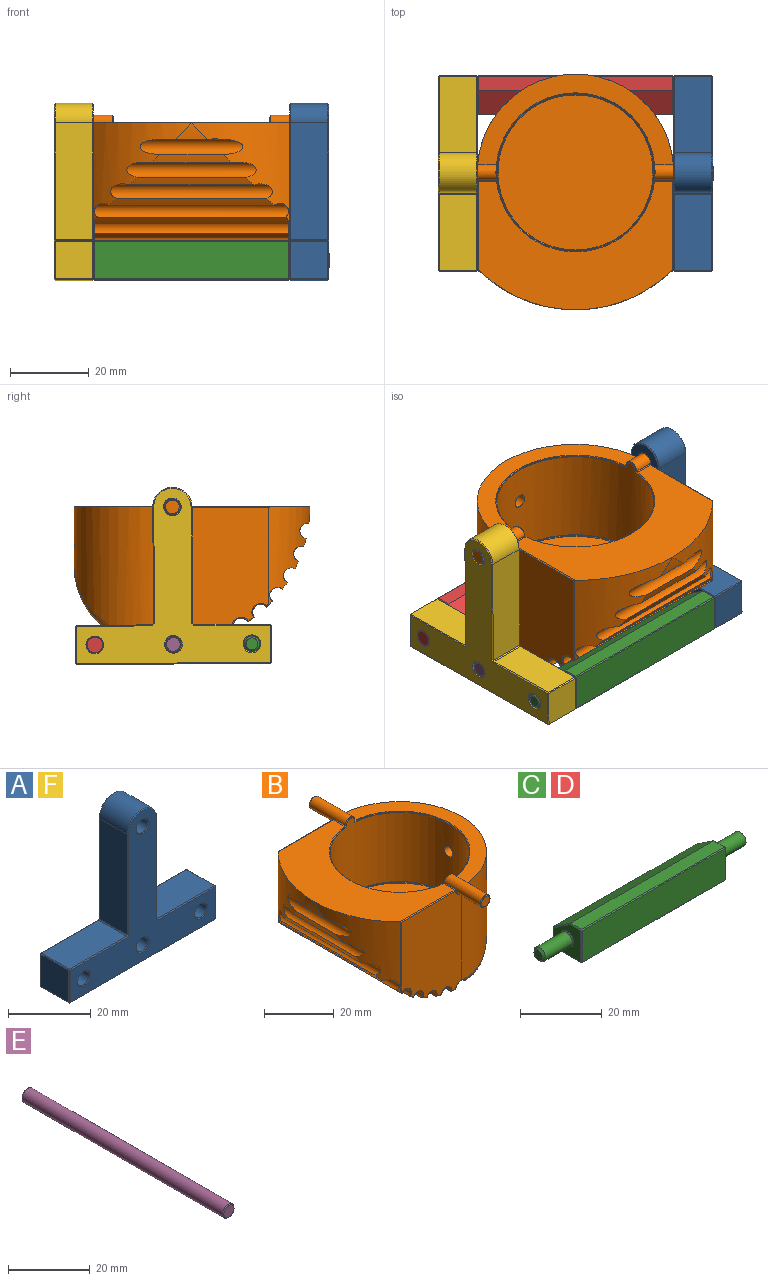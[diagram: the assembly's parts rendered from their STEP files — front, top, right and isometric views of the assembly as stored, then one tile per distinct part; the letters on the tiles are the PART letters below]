
ASSEMBLY  parts=6 mates=6
PART A: 56 faces, bbox 50x10x45 mm
  f0: plane 49.5x44.5mm, normal (0,-1,0), area 729.7mm2, adj f14,f17,f18,f21,f22,f27,f31,f32
  f1: plane 49.5x44.5mm, normal (0,1,0), area 729.7mm2, adj f16,f19,f20,f24,f25,f30,f34,f35
  f2: plane 29.75x9.5mm, normal (1,0,0), area 282.6mm2, adj f3,f14,f15,f16
  f3: cylinder r=5mm len=10mm, axis (0,1,0), area 149.2mm2, adj f2,f4,f17,f20
  f4: plane 29.75x9.5mm, normal (-1,0,0), area 282.6mm2, adj f3,f21,f25,f26
  f5: plane 19.5x9.5mm, normal (0,0,1), area 185.2mm2, adj f26,f31,f35,f36
  f6: plane 9.5x9.5mm, normal (-1,0,0), area 90.3mm2, adj f36,f41,f44,f47
  f7: plane 49.5x9.5mm, normal (0,0,-1), area 470.2mm2, adj f33,f42,f43,f47
  f8: plane 9.5x9.5mm, normal (1,0,0), area 90.3mm2, adj f23,f32,f33,f34
  f9: cylinder r=2mm len=9.5mm, axis (0,1,0), area 119.4mm2, adj f48,f52
  f10: cylinder r=2mm len=9.5mm, axis (0,1,0), area 119.4mm2, adj f49,f53
  f11: cylinder r=2mm len=9.5mm, axis (0,1,0), area 119.4mm2, adj f50,f54
  f12: plane 19.5x9.5mm, normal (0,0,1), area 185.2mm2, adj f15,f22,f23,f24
  f13: cylinder r=2mm len=9.5mm, axis (0,1,0), area 119.4mm2, adj f51,f55
  f14: plane 29.75x0.25mm, normal (0.71,-0.71,0), area 10.5mm2, adj f0,f2,f17,f18
  f15: plane 9.5x0.25mm, normal (0.71,0,0.71), area 3.4mm2, adj f2,f12,f18,f19
  f16: plane 29.75x0.25mm, normal (0.71,0.71,0), area 10.5mm2, adj f1,f2,f19,f20
  f17: cone r=4.75mm half-angle=45deg, axis (0,1,0), area 5.4mm2, adj f0,f3,f14,f21
  f18: plane 0.5x0.5mm, normal (0.58,-0.58,0.58), area 0.2mm2, adj f0,f14,f15,f22
  f19: plane 0.5x0.5mm, normal (0.58,0.58,0.58), area 0.2mm2, adj f1,f15,f16,f24
  f20: cone r=5mm half-angle=45deg, axis (0,-1,0), area 5.4mm2, adj f1,f3,f16,f25
  f21: plane 29.75x0.25mm, normal (-0.71,-0.71,0), area 10.5mm2, adj f0,f4,f17,f27
  f22: plane 19.5x0.25mm, normal (0,-0.71,0.71), area 6.9mm2, adj f0,f12,f18,f28
  f23: plane 9.5x0.25mm, normal (0.71,0,0.71), area 3.4mm2, adj f8,f12,f28,f29
  f24: plane 19.5x0.25mm, normal (0,0.71,0.71), area 6.9mm2, adj f1,f12,f19,f29
  f25: plane 29.75x0.25mm, normal (-0.71,0.71,0), area 10.5mm2, adj f1,f4,f20,f30
  f26: plane 9.5x0.25mm, normal (-0.71,0,0.71), area 3.4mm2, adj f4,f5,f27,f30
  f27: plane 0.5x0.5mm, normal (-0.58,-0.58,0.58), area 0.2mm2, adj f0,f21,f26,f31
  f28: plane 0.25x0.25mm, normal (0.58,-0.58,0.58), area 0.1mm2, adj f22,f23,f32
  f29: plane 0.25x0.25mm, normal (0.58,0.58,0.58), area 0.1mm2, adj f23,f24,f34
  f30: plane 0.5x0.5mm, normal (-0.58,0.58,0.58), area 0.2mm2, adj f1,f25,f26,f35
  f31: plane 19.5x0.25mm, normal (0,-0.71,0.71), area 6.9mm2, adj f0,f5,f27,f37
  f32: plane 9.5x0.25mm, normal (0.71,-0.71,0), area 3.4mm2, adj f0,f8,f28,f38
  f33: plane 9.5x0.25mm, normal (0.71,0,-0.71), area 3.4mm2, adj f7,f8,f38,f39
  f34: plane 9.5x0.25mm, normal (0.71,0.71,0), area 3.4mm2, adj f1,f8,f29,f39
  f35: plane 19.5x0.25mm, normal (0,0.71,0.71), area 6.9mm2, adj f1,f5,f30,f40
  f36: plane 9.5x0.25mm, normal (-0.71,0,0.71), area 3.4mm2, adj f5,f6,f37,f40
  f37: plane 0.25x0.25mm, normal (-0.58,-0.58,0.58), area 0.1mm2, adj f31,f36,f41
  f38: plane 0.25x0.25mm, normal (0.58,-0.58,-0.58), area 0.1mm2, adj f32,f33,f42
  f39: plane 0.25x0.25mm, normal (0.58,0.58,-0.58), area 0.1mm2, adj f33,f34,f43
  f40: plane 0.25x0.25mm, normal (-0.58,0.58,0.58), area 0.1mm2, adj f35,f36,f44
  f41: plane 9.5x0.25mm, normal (-0.71,-0.71,0), area 3.4mm2, adj f0,f6,f37,f45
  f42: plane 49.5x0.25mm, normal (0,-0.71,-0.71), area 17.5mm2, adj f0,f7,f38,f45
  f43: plane 49.5x0.25mm, normal (0,0.71,-0.71), area 17.5mm2, adj f1,f7,f39,f46
  f44: plane 9.5x0.25mm, normal (-0.71,0.71,0), area 3.4mm2, adj f1,f6,f40,f46
  f45: plane 0.25x0.25mm, normal (-0.58,-0.58,-0.58), area 0.1mm2, adj f41,f42,f47
  f46: plane 0.25x0.25mm, normal (-0.58,0.58,-0.58), area 0.1mm2, adj f43,f44,f47
  f47: plane 9.5x0.25mm, normal (-0.71,0,-0.71), area 3.4mm2, adj f6,f7,f45,f46
  f48: cone r=2mm half-angle=45deg, axis (0,1,0), area 4.7mm2, adj f1,f9
  f49: cone r=2.25mm half-angle=45deg, axis (0,1,0), area 4.7mm2, adj f1,f10
  f50: cone r=2.25mm half-angle=45deg, axis (0,1,0), area 4.7mm2, adj f1,f11
  f51: cone r=2.25mm half-angle=45deg, axis (0,1,0), area 4.7mm2, adj f1,f13
  f52: cone r=2.25mm half-angle=45deg, axis (0,-1,0), area 4.7mm2, adj f0,f9
  f53: cone r=2mm half-angle=45deg, axis (0,-1,0), area 4.7mm2, adj f0,f10
  f54: cone r=2mm half-angle=45deg, axis (0,-1,0), area 4.7mm2, adj f0,f11
  f55: cone r=2mm half-angle=45deg, axis (0,-1,0), area 4.7mm2, adj f0,f13
PART B: 89 faces, bbox 60x70x37.2 mm
  f0: cylinder r=25mm len=50mm, axis (0,0,1), area 2123.7mm2, adj f12,f16,f17,f45,f61,f62,f78,f79
  f1: cylinder r=20mm len=40mm, axis (0,0,1), area 3054.9mm2, adj f2,f30,f31,f32,f33,f34,f88
  f2: cylinder r=20mm len=0.7mm, axis (0,0,1), area 0mm2, adj f1,f32
  f3: cylinder r=35mm len=8.2mm, axis (0,1,0), area 16.8mm2, adj f20,f21,f44
  f4: cylinder r=35mm len=20.15mm, axis (0,1,0), area 38.2mm2, adj f20,f21,f43,f44
  f5: cylinder r=35mm len=31.48mm, axis (0,1,0), area 62.3mm2, adj f20,f21,f42,f43
  f6: cylinder r=35mm len=41.86mm, axis (0,1,0), area 84.6mm2, adj f20,f21,f41,f42
  f7: cylinder r=35mm len=49.5mm, axis (0,1,0), area 103.6mm2, adj f20,f21,f40,f41,f51,f68
  f8: cylinder r=35mm len=49.5mm, axis (0,1,0), area 104.4mm2, adj f39,f40,f53,f70
  f9: cylinder r=35mm len=49.5mm, axis (0,1,0), area 104.4mm2, adj f38,f39,f55,f72
  f10: cylinder r=35mm len=49.5mm, axis (0,1,0), area 104.4mm2, adj f37,f38,f57,f74
  f11: plane 45.48x1.54mm, normal (0,0,-1), area 69.4mm2, adj f18,f81,f84,f87
  f12: plane 50.31x23.03mm, normal (0,0,1), area 318.6mm2, adj f0,f22,f24,f25,f28,f32,f45,f62
  f13: cone r=20mm half-angle=45deg, axis (0,0,1), area 14.8mm2, adj f14,f25,f30,f32
  f14: plane 49.5x33.03mm, normal (0,0,1), area 910.3mm2, adj f13,f20,f21,f25,f32,f47,f49,f63
  f15: cylinder r=35mm len=49.5mm, axis (0,1,0), area 104.4mm2, adj f36,f37,f59,f76
  f16: plane 34.43x24.39mm, normal (0,1,0), area 731.9mm2, adj f0,f46,f49,f50,f51,f52,f53,f54
  f17: plane 34.43x24.39mm, normal (0,-1,0), area 731.9mm2, adj f0,f64,f66,f67,f68,f69,f70,f71
  f18: cylinder r=20mm len=44.9mm, axis (0,1,0), area 705.3mm2, adj f11,f79,f80
  f19: plane 39.5x39.5mm, normal (0,0,1), area 1225.4mm2, adj f26
  f20: cylinder r=35mm len=24.93mm, axis (0,0,1), area 304.3mm2, adj f3,f4,f5,f6,f7,f14,f41,f42
  f21: cylinder r=35mm len=24.93mm, axis (0,0,1), area 304.2mm2, adj f3,f4,f5,f6,f7,f14,f41,f42
  f22: cylinder r=2mm len=14.58mm, axis (0,1,0), area 150.4mm2, adj f12,f25,f27,f62,f63,f64,f65
  f23: plane 3.5x3.5mm, normal (0,-1,0), area 9.6mm2, adj f27
  f24: cone r=20mm half-angle=45deg, axis (0,0,1), area 14.8mm2, adj f12,f25,f32,f33
  f25: bspline ~4.7x2.91mm, area 1.6mm2, adj f12,f13,f14,f22,f24,f31,f63
  f26: cone r=19.75mm half-angle=45deg, axis (0,0,1), area 31.2mm2, adj f19,f34
  f27: cone r=1.75mm half-angle=45deg, axis (0,1,0), area 4.2mm2, adj f22,f23
  f28: cylinder r=2mm len=14.58mm, axis (0,-1,0), area 150.4mm2, adj f12,f32,f35,f45,f46,f47,f48
  f29: plane 3.5x3.5mm, normal (0,1,0), area 9.6mm2, adj f35
  f30: cone r=20mm half-angle=22.5deg, axis (0,0,1), area 11.4mm2, adj f1,f13,f31,f32
  f31: bspline ~3.61x2.21mm, area 1.1mm2, adj f1,f25,f30,f33
  f32: bspline ~4.71x3.04mm, area 2.2mm2, adj f1,f2,f12,f13,f14,f24,f28,f30
  f33: cone r=20mm half-angle=22.5deg, axis (0,0,1), area 11.4mm2, adj f1,f24,f31,f32
  f34: cone r=20mm half-angle=22.5deg, axis (0,0,1), area 24mm2, adj f1,f26
  f35: cone r=2mm half-angle=45deg, axis (0,-1,0), area 4.2mm2, adj f28,f29
  f36: cylinder r=2mm len=49.5mm, axis (0,-1,0), area 256mm2, adj f15,f60,f61,f77,f78,f82,f83,f87
  f37: cylinder r=2mm len=49.5mm, axis (0,-1,0), area 305.4mm2, adj f10,f15,f58,f75
  f38: cylinder r=2mm len=49.5mm, axis (0,-1,0), area 305.4mm2, adj f9,f10,f56,f73
  f39: cylinder r=2mm len=49.5mm, axis (0,-1,0), area 305.4mm2, adj f8,f9,f54,f71
  f40: cylinder r=2mm len=49.5mm, axis (0,-1,0), area 305.4mm2, adj f7,f8,f52,f69
  f41: cylinder r=2mm len=47.98mm, axis (0,-1,0), area 277.1mm2, adj f6,f7,f20,f21
  f42: cylinder r=2mm len=38.41mm, axis (0,-1,0), area 215.6mm2, adj f5,f6,f20,f21
  f43: cylinder r=2mm len=32.92mm, axis (0,-1,0), area 182.4mm2, adj f4,f5,f20,f21
  f44: cylinder r=2mm len=26.14mm, axis (0,-1,0), area 134.1mm2, adj f3,f4,f20,f21
  f45: bspline ~2.63x2.56mm, area 1.3mm2, adj f0,f12,f28,f46
  f46: torus R=2.25mm, axis (0,-1,0), area 1.2mm2, adj f16,f28,f45,f48
  f47: cylinder r=0.25mm len=4.57mm, axis (0,-1,0), area 1.6mm2, adj f14,f28,f32,f48
  f48: bspline ~0.58x0.54mm, area 0.2mm2, adj f28,f46,f47,f49
  f49: cylinder r=0.25mm len=22.51mm, axis (-1,0,0), area 8.8mm2, adj f14,f16,f21,f48,f50
  f50: cylinder r=0.25mm len=24.75mm, axis (0,0,1), area 4.8mm2, adj f16,f21,f49,f51
  f51: torus R=34.75mm, axis (0,-1,0), area 0.3mm2, adj f7,f16,f21,f50,f52
  f52: torus R=2.25mm, axis (0,-1,0), area 2.4mm2, adj f16,f40,f51,f53
  f53: torus R=34.75mm, axis (0,-1,0), area 0.7mm2, adj f8,f16,f52,f54
  f54: torus R=2.25mm, axis (0,-1,0), area 2.4mm2, adj f16,f39,f53,f55
  f55: torus R=34.75mm, axis (0,-1,0), area 0.7mm2, adj f9,f16,f54,f56
  f56: torus R=2.25mm, axis (0,-1,0), area 2.4mm2, adj f16,f38,f55,f57
  f57: torus R=34.75mm, axis (0,-1,0), area 0.7mm2, adj f10,f16,f56,f58
  f58: torus R=2.25mm, axis (0,-1,0), area 2.4mm2, adj f16,f37,f57,f59
  f59: torus R=34.75mm, axis (0,-1,0), area 0.7mm2, adj f15,f16,f58,f60
  f60: torus R=2.25mm, axis (0,-1,0), area 1.2mm2, adj f16,f36,f59,f61
  f61: bspline ~1.34x0.56mm, area 0.4mm2, adj f0,f36,f60,f82
  f62: bspline ~2.63x2.56mm, area 1.3mm2, adj f0,f12,f22,f64
  f63: cylinder r=0.25mm len=4.57mm, axis (0,1,0), area 1.6mm2, adj f14,f22,f25,f65
  f64: torus R=2.25mm, axis (0,-1,0), area 1.2mm2, adj f17,f22,f62,f65
  f65: bspline ~0.61x0.52mm, area 0.2mm2, adj f22,f63,f64,f66
  f66: cylinder r=0.25mm len=22.51mm, axis (1,0,0), area 8.8mm2, adj f14,f17,f20,f65,f67
  f67: cylinder r=0.25mm len=24.75mm, axis (0,0,1), area 4.8mm2, adj f17,f20,f66,f68
  f68: torus R=34.75mm, axis (0,-1,0), area 0.3mm2, adj f7,f17,f20,f67,f69
  f69: torus R=2.25mm, axis (0,-1,0), area 2.4mm2, adj f17,f40,f68,f70
  f70: torus R=34.75mm, axis (0,-1,0), area 0.7mm2, adj f8,f17,f69,f71
  f71: torus R=2.25mm, axis (0,-1,0), area 2.4mm2, adj f17,f39,f70,f72
  f72: torus R=34.75mm, axis (0,-1,0), area 0.7mm2, adj f9,f17,f71,f73
  f73: torus R=2.25mm, axis (0,-1,0), area 2.4mm2, adj f17,f38,f72,f74
  f74: torus R=34.75mm, axis (0,-1,0), area 0.7mm2, adj f10,f17,f73,f75
  f75: torus R=2.25mm, axis (0,-1,0), area 2.4mm2, adj f17,f37,f74,f76
  f76: torus R=34.75mm, axis (0,-1,0), area 0.7mm2, adj f15,f17,f75,f77
  f77: torus R=2.25mm, axis (0,-1,0), area 1.2mm2, adj f17,f36,f76,f78
  f78: bspline ~1.34x0.56mm, area 0.4mm2, adj f0,f36,f77,f83
  f79: bspline ~24.62x20.91mm, area 46.2mm2, adj f0,f18,f81
  f80: bspline ~24.98x23.64mm, area 46.2mm2, adj f0,f18,f84
  f81: torus R=23mm, axis (0,0,1), area 9.4mm2, adj f0,f11,f79,f82,f85
  f82: bspline ~1.6x1.57mm, area 0.5mm2, adj f36,f61,f81,f85
  f83: bspline ~1.6x1.57mm, area 0.5mm2, adj f36,f78,f84,f86
  f84: torus R=23mm, axis (0,0,1), area 9.4mm2, adj f0,f11,f80,f83,f86
  f85: bspline ~2.06x1.87mm, area 0.3mm2, adj f81,f82,f87
  f86: bspline ~2.06x1.87mm, area 0.3mm2, adj f83,f84,f87
  f87: cylinder r=2mm len=48.88mm, axis (0,-1,0), area 98.8mm2, adj f11,f36,f85,f86
  f88: cylinder r=1.7mm len=5mm, axis (1,0,0), area 53.4mm2, adj f0,f1
PART C: 33 faces, bbox 70x10x10 mm
  f0: plane 49.5x9.5mm, normal (0,0,-1), area 470.2mm2, adj f19,f24,f27,f30
  f1: plane 9.5x9.5mm, normal (1,0,0), area 63mm2, adj f15,f16,f21,f24,f25,f31
  f2: plane 49.5x3.75mm, normal (0,0,1), area 185.6mm2, adj f11,f12,f16,f17
  f3: plane 9.5x9.5mm, normal (-1,0,0), area 63mm2, adj f17,f18,f22,f26,f27,f32
  f4: plane 49.5x9.5mm, normal (0,-1,0), area 470.2mm2, adj f12,f15,f18,f19
  f5: plane 49.5x5.75mm, normal (0,1,0), area 284.6mm2, adj f11,f25,f26,f30
  f6: cylinder r=2mm len=9.25mm, axis (1,0,0), area 116.2mm2, adj f8,f32
  f7: plane 3x3mm, normal (-1,0,0), area 7.1mm2, adj f8
  f8: cone r=1.5mm half-angle=45deg, axis (1,0,0), area 7.8mm2, adj f6,f7
  f9: cylinder r=2mm len=9.75mm, axis (-1,0,0), area 122.5mm2, adj f10,f31
  f10: plane 4x4mm, normal (1,0,0), area 12.6mm2, adj f9
  f11: plane 49.5x6mm, normal (0,0.55,0.83), area 356.9mm2, adj f2,f5,f21,f22
  f12: plane 49.5x0.25mm, normal (0,-0.71,0.71), area 17.5mm2, adj f2,f4,f13,f14
  f13: plane 0.25x0.25mm, normal (0.58,-0.58,0.58), area 0.1mm2, adj f12,f15,f16
  f14: plane 0.25x0.25mm, normal (-0.58,-0.58,0.58), area 0.1mm2, adj f12,f17,f18
  f15: plane 9.5x0.25mm, normal (0.71,-0.71,0), area 3.4mm2, adj f1,f4,f13,f20
  f16: plane 3.75x0.25mm, normal (0.71,0,0.71), area 1.3mm2, adj f1,f2,f13,f21
  f17: plane 3.75x0.25mm, normal (-0.71,0,0.71), area 1.3mm2, adj f2,f3,f14,f22
  f18: plane 9.5x0.25mm, normal (-0.71,-0.71,0), area 3.4mm2, adj f3,f4,f14,f23
  f19: plane 49.5x0.25mm, normal (0,-0.71,-0.71), area 17.5mm2, adj f0,f4,f20,f23
  f20: plane 0.25x0.25mm, normal (0.58,-0.58,-0.58), area 0.1mm2, adj f15,f19,f24
  f21: plane 6.08x4.13mm, normal (0.71,0.39,0.59), area 2.5mm2, adj f1,f11,f16,f25
  f22: plane 6.08x4.13mm, normal (-0.71,0.39,0.59), area 2.5mm2, adj f3,f11,f17,f26
  f23: plane 0.25x0.25mm, normal (-0.58,-0.58,-0.58), area 0.1mm2, adj f18,f19,f27
  f24: plane 9.5x0.25mm, normal (0.71,0,-0.71), area 3.4mm2, adj f0,f1,f20,f28
  f25: plane 5.75x0.25mm, normal (0.71,0.71,0), area 2mm2, adj f1,f5,f21,f28
  f26: plane 5.75x0.25mm, normal (-0.71,0.71,0), area 2mm2, adj f3,f5,f22,f29
  f27: plane 9.5x0.25mm, normal (-0.71,0,-0.71), area 3.4mm2, adj f0,f3,f23,f29
  f28: plane 0.25x0.25mm, normal (0.58,0.58,-0.58), area 0.1mm2, adj f24,f25,f30
  f29: plane 0.25x0.25mm, normal (-0.58,0.58,-0.58), area 0.1mm2, adj f26,f27,f30
  f30: plane 49.5x0.25mm, normal (0,0.71,-0.71), area 17.5mm2, adj f0,f5,f28,f29
  f31: cone r=2.25mm half-angle=45deg, axis (-1,0,0), area 4.7mm2, adj f1,f9
  f32: cone r=2mm half-angle=45deg, axis (1,0,0), area 4.7mm2, adj f3,f6
PART D: same geometry as C
PART E: 5 faces, bbox 4x70x4 mm
  f0: cylinder r=2mm len=69.5mm, axis (0,1,0), area 873.4mm2, adj f3,f4
  f1: plane 3.5x3.5mm, normal (0,-1,0), area 9.6mm2, adj f3
  f2: plane 3.5x3.5mm, normal (0,1,0), area 9.6mm2, adj f4
  f3: cone r=1.75mm half-angle=45deg, axis (0,1,0), area 4.2mm2, adj f0,f1
  f4: cone r=2mm half-angle=45deg, axis (0,-1,0), area 4.2mm2, adj f0,f2
PART F: same geometry as A
PLACE A rot(axis=(0,0,1),90deg) t=(52.06,0,19.85)mm fixed
PLACE B rot(axis=(0,0,1),90deg) t=(22.06,0,19.85)mm
PLACE C rot(axis=(-1,0,0),0.4deg) t=(22.06,-20.25,-15.01)mm
PLACE D rot(axis=(0,0,1),180deg) t=(22.06,19.75,-15.3)mm
PLACE E rot(axis=(0,0,1),90deg) t=(22.31,-0.25,-15.15)mm
PLACE F rot(axis=(0,0,1),90deg) t=(-7.94,0,19.85)mm
MATE fastened D.f6 <-> A.f9  axis (1,0,0) through (47.06,19.75,-15.3)mm
MATE fastened C.f6 <-> A.f10  axis (1,0,0) through (47.06,-20.25,-15.01)mm
MATE revolute F.f13 <-> B.f22  axis (1,0,0) through (-2.94,0,19.85)mm
MATE slider E.f0 <-> A.f11  axis (1,0,0) through (57.31,-0.25,-15.15)mm
MATE revolute B.f22 <-> A.f3  axis (1,0,0) through (57.06,0,19.85)mm
MATE slider F.f11 <-> E.f0  axis (-1,0,0) through (-12.94,-0.25,-15.15)mm
